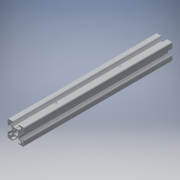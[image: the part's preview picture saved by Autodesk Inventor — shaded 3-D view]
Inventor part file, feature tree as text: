
AUTODESK INVENTOR PART (.ipt)
format: ipt  version: 2016 (Build 200138000, 138)  size: 409,600 bytes
history: native  units: in
note: dims shown in document units (in); Inventor stores cm internally (conversion verified against a paired STEP export)
features: other x3, sketch x2, extrude x1, hole x1, mirror x1
ambient origin geometry x8: Origin, YZ Plane, XZ Plane, XY Plane, X Axis, Y Axis, Z Axis, Center Point
bodies: Solid1 (feature_tree)
feature tree (8):
  other  "Blocks"
  extrude  "Extrusion1"  Depth=2.0in
  hole  "Hole1"  [1 undecoded]
  mirror  "Mirror1"
  sketch  "Sketch1"  dims[d1=0.0in d5=2.0in]
  other  "20x20"
  sketch  "Sketch3"  dims[d6=0.187in d7=0.75in d8=0.375in d9=0.25in d10=0.5635in d11=1.0in d12=0.8108in d13=1.0in d14=1.0in]
  other  "20x20:1"
note: 1 required parameter value undecoded (feature->parameter linkage not recoverable at this tier; creation-order binding heuristic only, values carry confidence <= 0.55)
